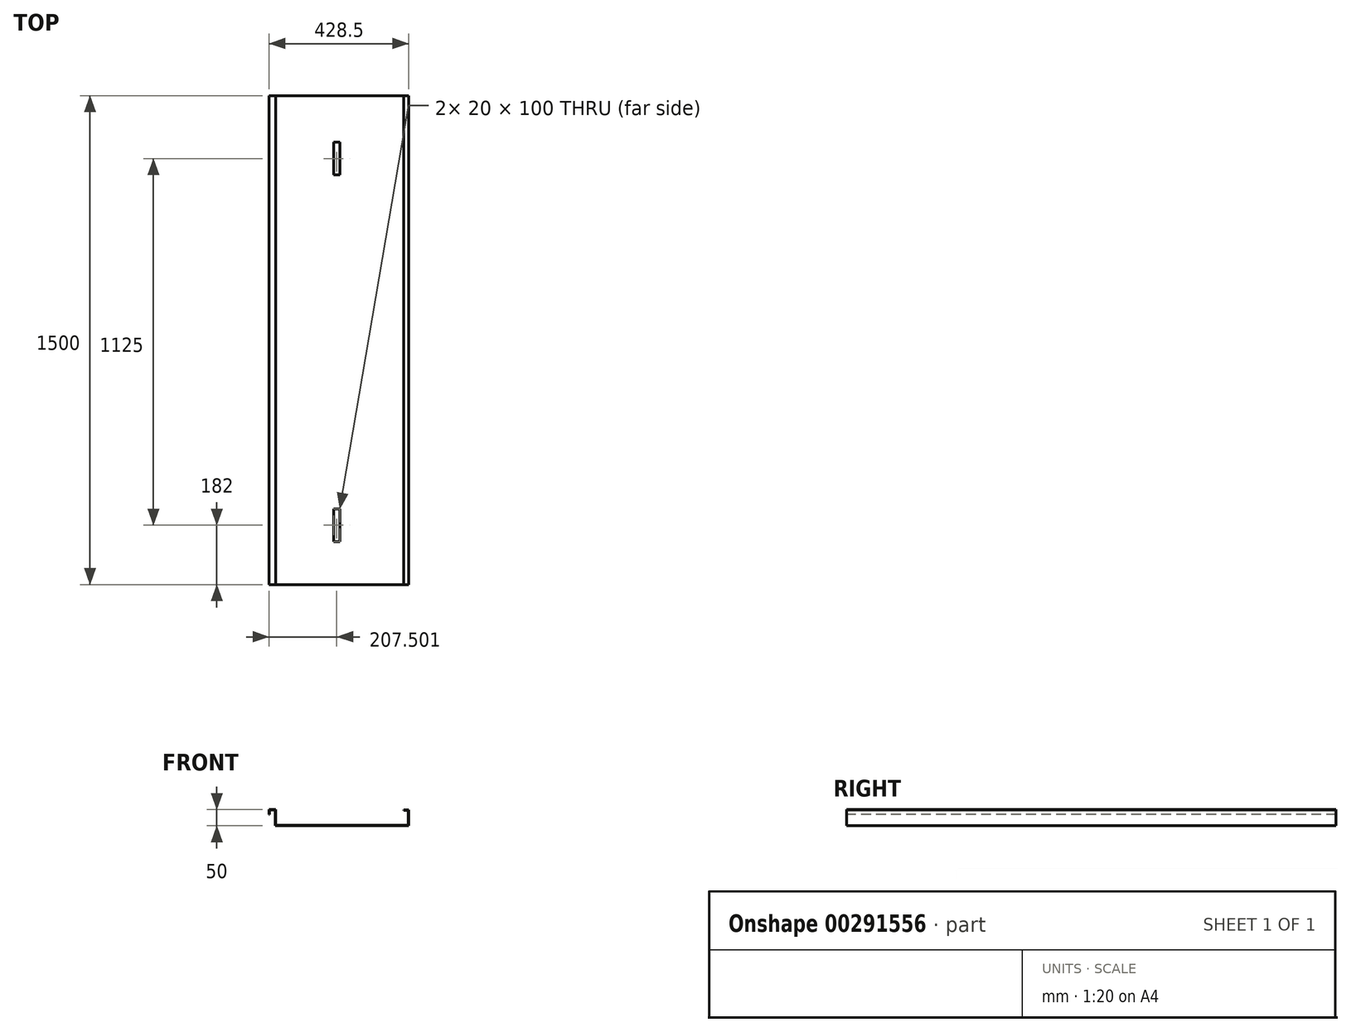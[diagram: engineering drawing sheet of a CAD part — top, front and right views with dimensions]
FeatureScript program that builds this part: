
annotation { "Feature Type Name" : "Feature", "Feature Type Description" : "" }
export const myFeature = defineFeature(function(context is Context, id is Id, definition is map)
    precondition{}
    {
        {
            var Q0;
            Q0=qCreatedBy(makeId("Front.planeOp"),FACE);
            var sketch = newSketch(context, id + "F0", { "sketchPlane" : qUnion([Q0])});
            skLineSegment(sketch, "E0", {"start": v(9.56, 16.63) * mm, "end": v(419.56, 16.63) * mm});
            skLineSegment(sketch, "E1", {"start": v(419.56, 16.63) * mm, "end": v(419.56, 65.13) * mm});
            skLineSegment(sketch, "E2", {"start": v(419.56, 65.13) * mm, "end": v(403.56, 65.13) * mm});
            skLineSegment(sketch, "E3", {"start": v(403.56, 65.13) * mm, "end": v(403.56, 63.63) * mm});
            skLineSegment(sketch, "E4", {"start": v(403.56, 63.63) * mm, "end": v(418.06, 63.63) * mm});
            skLineSegment(sketch, "E5", {"start": v(9.56, 16.63) * mm, "end": v(9.56, 65.13) * mm});
            skLineSegment(sketch, "E6", {"start": v(418.06, 63.63) * mm, "end": v(418.06, 18.13) * mm});
            skLineSegment(sketch, "E7", {"start": v(418.06, 18.13) * mm, "end": v(11.06, 18.13) * mm});
            skLineSegment(sketch, "E8", {"start": v(11.06, 18.13) * mm, "end": v(11.06, 66.63) * mm});
            skLineSegment(sketch, "E9", {"start": v(11.06, 66.63) * mm, "end": v(-8.94, 66.63) * mm});
            skLineSegment(sketch, "E10", {"start": v(-8.94, 66.63) * mm, "end": v(-8.94, 51.63) * mm});
            skLineSegment(sketch, "E11", {"start": v(-8.94, 51.63) * mm, "end": v(-7.44, 51.63) * mm});
            skLineSegment(sketch, "E12", {"start": v(-7.44, 51.63) * mm, "end": v(-7.44, 65.13) * mm});
            skLineSegment(sketch, "E13", {"start": v(-7.44, 65.13) * mm, "end": v(9.56, 65.13) * mm});
            skSolve(sketch);
        }
        {
            var Q0;
            Q0=makeQuery(id+"F0.imprint","IMPRINT",FACE,{"disambiguationData":[TD([[makeQuery(id+"F0.imprint","IMPRINT",EDGE,{"derivedFrom":sQuery(id+"F0.wireOp",EDGE,"E0")}),1.0]])]});
            extrude(context, id + "F1", {"entities" : qUnion([Q0]), "oppositeDirection" : true, "depth" : 1500 * mm});
        }
        {
            var Q0;
            Q0=makeQuery(id+"F1.opExtrude","SWEPT_FACE",FACE,{"disambiguationData":[OSD([sQuery(id+"F0.wireOp",EDGE,"E7")])]});
            var sketch = newSketch(context, id + "F2", { "sketchPlane" : qUnion([Q0])});
            skLineSegment(sketch, "E14.bottom", {"start": v(188.56, 232) * mm, "end": v(208.56, 232) * mm});
            skLineSegment(sketch, "E14.top", {"start": v(188.56, 132) * mm, "end": v(208.56, 132) * mm});
            skLineSegment(sketch, "E14.left", {"start": v(188.56, 232) * mm, "end": v(188.56, 132) * mm});
            skLineSegment(sketch, "E14.right", {"start": v(208.56, 232) * mm, "end": v(208.56, 132) * mm});
            skLineSegment(sketch, "E15", {"start": v(198.56, 182) * mm, "end": v(198.56, 1357) * mm, "construction": true});
            skLineSegment(sketch, "E16", {"start": v(188.56, 1357) * mm, "end": v(188.56, 1257) * mm});
            skLineSegment(sketch, "E17", {"start": v(188.56, 1257) * mm, "end": v(208.56, 1257) * mm});
            skLineSegment(sketch, "E18", {"start": v(208.56, 1257) * mm, "end": v(208.56, 1357) * mm});
            skLineSegment(sketch, "E19", {"start": v(188.56, 1357) * mm, "end": v(208.56, 1357) * mm});
            skSolve(sketch);
        }
        {
            var Q0;
            Q0=makeQuery(id+"F2.imprint","IMPRINT",FACE,{"disambiguationData":[TD([[makeQuery(id+"F2.imprint","IMPRINT",EDGE,{"derivedFrom":sQuery(id+"F2.wireOp",EDGE,"E14.bottom")}),-1.0]])]});
            var Q1;
            Q1=makeQuery(id+"F2.imprint","IMPRINT",FACE,{"disambiguationData":[TD([[makeQuery(id+"F2.imprint","IMPRINT",EDGE,{"derivedFrom":sQuery(id+"F2.wireOp",EDGE,"E16")}),1.0]])]});
            extrude(context, id + "F3", {"entities" : qUnion([Q0, Q1]), "operationType" : NewBodyOperationType.REMOVE, "endBound" : BoundingType.UP_TO_NEXT, "oppositeDirection" : true, "depth" : 25 * mm});
        }
    });
